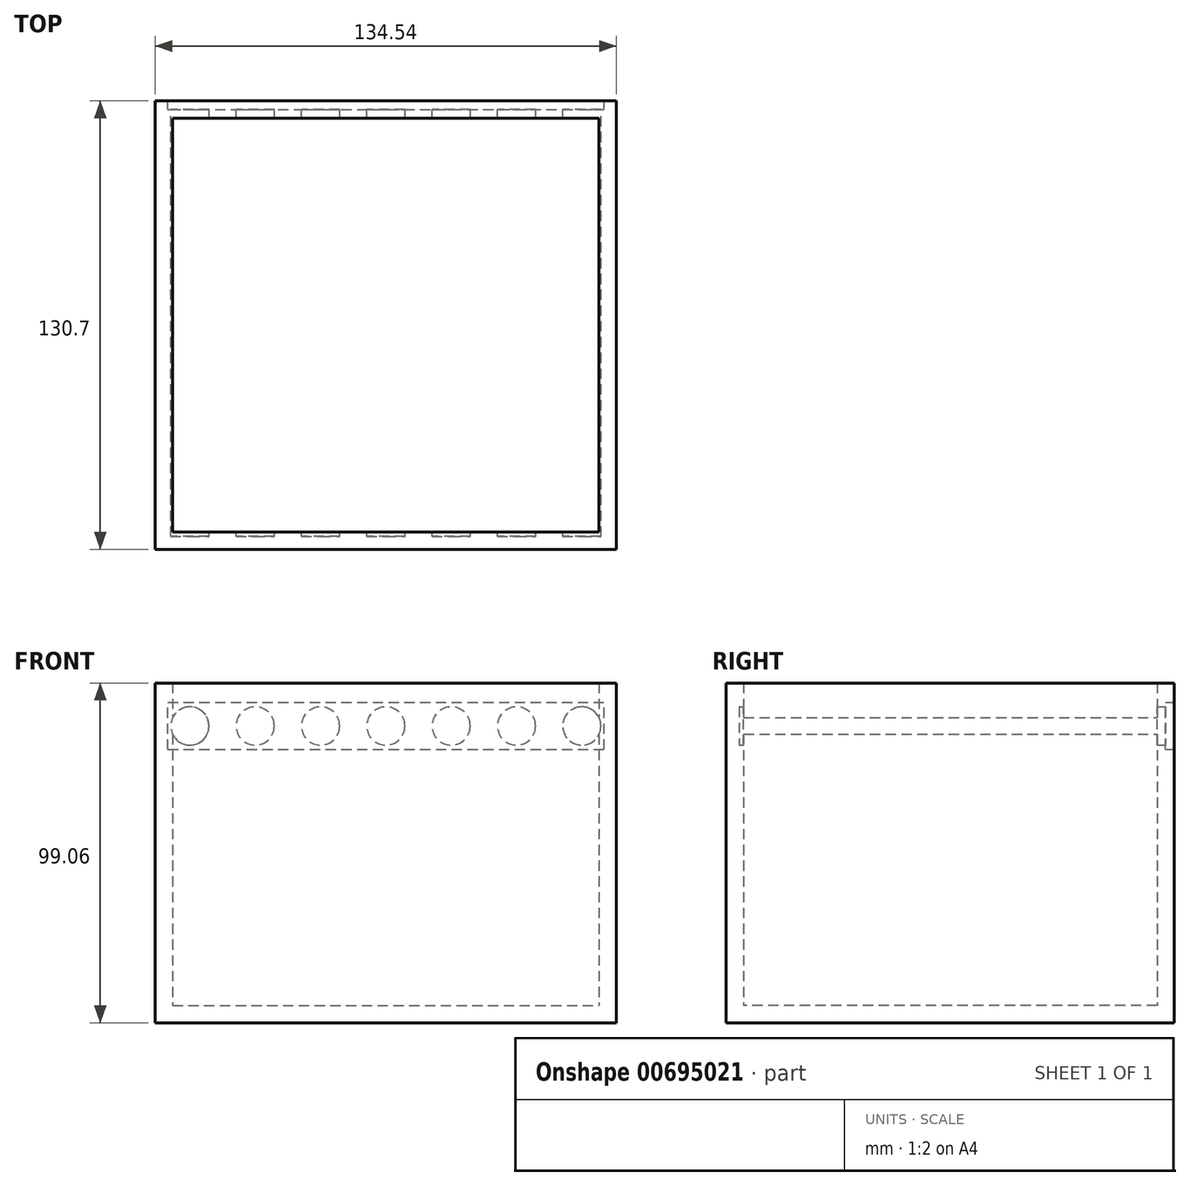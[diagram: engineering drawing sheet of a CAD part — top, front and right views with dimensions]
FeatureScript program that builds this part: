
annotation { "Feature Type Name" : "Feature", "Feature Type Description" : "" }
export const myFeature = defineFeature(function(context is Context, id is Id, definition is map)
    precondition{}
    {
        {
            var Q0;
            Q0=qCreatedBy(makeId("Top.planeOp"),FACE);
            var sketch = newSketch(context, id + "F0", { "sketchPlane" : qUnion([Q0])});
            skLineSegment(sketch, "E0.bottom", {"start": v(-65.32, 63.82) * mm, "end": v(69.22, 63.82) * mm});
            skLineSegment(sketch, "E0.top", {"start": v(-65.32, -66.88) * mm, "end": v(69.22, -66.88) * mm});
            skLineSegment(sketch, "E0.left", {"start": v(-65.32, 63.82) * mm, "end": v(-65.32, -66.88) * mm});
            skLineSegment(sketch, "E0.right", {"start": v(69.22, 63.82) * mm, "end": v(69.22, -66.88) * mm});
            skSolve(sketch);
        }
        {
            var Q0;
            Q0=makeQuery(id+"F0.imprint","IMPRINT",FACE,{"disambiguationData":[TD([[makeQuery(id+"F0.imprint","IMPRINT",EDGE,{"derivedFrom":sQuery(id+"F0.wireOp",EDGE,"E0.bottom")}),-1.0]])]});
            extrude(context, id + "F1", {"entities" : qUnion([Q0]), "depth" : 99.06 * mm, "offsetDistance" : 25.4 * mm});
        }
        {
            var Q0;
            Q0=makeQuery(id+"F1.opExtrude","CAP_FACE",FACE,{"disambiguationData":[OSD([sQuery(id+"F0.wireOp",EDGE,"E0.bottom"),sQuery(id+"F0.wireOp",EDGE,"E0.top"),sQuery(id+"F0.wireOp",EDGE,"E0.left"),sQuery(id+"F0.wireOp",EDGE,"E0.right")])],"isStart":false});
            shell(context, id + "F2", {"entities" : qUnion([Q0]), "thickness" : 5.08 * mm});
        }
        {
            var Q0;
            Q0=makeQuery(id+"F1.opExtrude","SWEPT_FACE",FACE,{"disambiguationData":[OSD([sQuery(id+"F0.wireOp",EDGE,"E0.bottom")])]});
            var sketch = newSketch(context, id + "F3", { "sketchPlane" : qUnion([Q0])});
            skLineSegment(sketch, "E1", {"start": v(65.32, 86.52) * mm, "end": v(-69.22, 86.52) * mm, "construction": true});
            skLineSegment(sketch, "E2", {"start": v(-1.95, 86.52) * mm, "end": v(-1.95, 0) * mm, "construction": true});
            skCircle(sketch, "E3", {"center": v(-1.95, 86.52) * mm, "radius": 5.59 * mm});
            skLineSegment(sketch, "E4", {"start": v(-11.48, 80.63) * mm, "end": v(-11.48, 90.02) * mm, "construction": true});
            skCircle(sketch, "E5.MirrorC", {"center": v(-21, 86.52) * mm, "radius": 5.59 * mm});
            skLineSegment(sketch, "E6", {"start": v(-21, 86.52) * mm, "end": v(-21, 80.93) * mm, "construction": true});
            skLineSegment(sketch, "E7", {"start": v(-21, 80.93) * mm, "end": v(-21, 92.1) * mm, "construction": true});
            skLineSegment(sketch, "E8.MirrorCS", {"start": v(-30.53, 80.63) * mm, "end": v(-30.53, 90.02) * mm, "construction": true});
            skCircle(sketch, "E9.MirrorC", {"center": v(-40.05, 86.52) * mm, "radius": 5.59 * mm});
            skLineSegment(sketch, "E10.MirrorCS", {"start": v(-40.05, 80.93) * mm, "end": v(-40.05, 92.1) * mm, "construction": true});
            skLineSegment(sketch, "E11.MirrorCS", {"start": v(-49.58, 80.63) * mm, "end": v(-49.58, 90.02) * mm, "construction": true});
            skCircle(sketch, "E12.MirrorC", {"center": v(-59.1, 86.52) * mm, "radius": 5.59 * mm});
            skCircle(sketch, "E13.MirrorC", {"center": v(17.1, 86.52) * mm, "radius": 5.59 * mm});
            skCircle(sketch, "E14.MirrorC", {"center": v(36.15, 86.52) * mm, "radius": 5.59 * mm});
            skCircle(sketch, "E15.MirrorC", {"center": v(55.2, 86.52) * mm, "radius": 5.59 * mm});
            skSolve(sketch);
        }
        {
            var Q0;
            Q0 = qSketchRegion(id + "F3", true);
            extrude(context, id + "F4", {"entities" : qUnion([Q0]), "operationType" : NewBodyOperationType.REMOVE, "oppositeDirection" : true, "depth" : 127 * mm, "offsetDistance" : 25.4 * mm});
        }
        {
            var Q0;
            Q0=makeQuery(id+"F1.opExtrude","SWEPT_FACE",FACE,{"disambiguationData":[OSD([sQuery(id+"F0.wireOp",EDGE,"E0.bottom")])]});
            var sketch = newSketch(context, id + "F5", { "sketchPlane" : qUnion([Q0])});
            skCircle(sketch, "E16.0", {"center": v(-1.95, 86.52) * mm, "radius": 5.59 * mm});
            skLineSegment(sketch, "E17.bottom", {"start": v(61.65, 79.66) * mm, "end": v(-65.55, 79.66) * mm});
            skLineSegment(sketch, "E17.top", {"start": v(61.65, 93.38) * mm, "end": v(-65.55, 93.38) * mm});
            skLineSegment(sketch, "E17.left", {"start": v(61.65, 79.66) * mm, "end": v(61.65, 93.38) * mm});
            skLineSegment(sketch, "E17.right", {"start": v(-65.55, 79.66) * mm, "end": v(-65.55, 93.38) * mm});
            skSolve(sketch);
        }
        {
            var Q0;
            Q0 = qSketchRegion(id + "F5", true);
            extrude(context, id + "F6", {"entities" : qUnion([Q0]), "operationType" : NewBodyOperationType.REMOVE, "oppositeDirection" : true, "depth" : 2.54 * mm, "offsetDistance" : 25.4 * mm});
        }
    });
